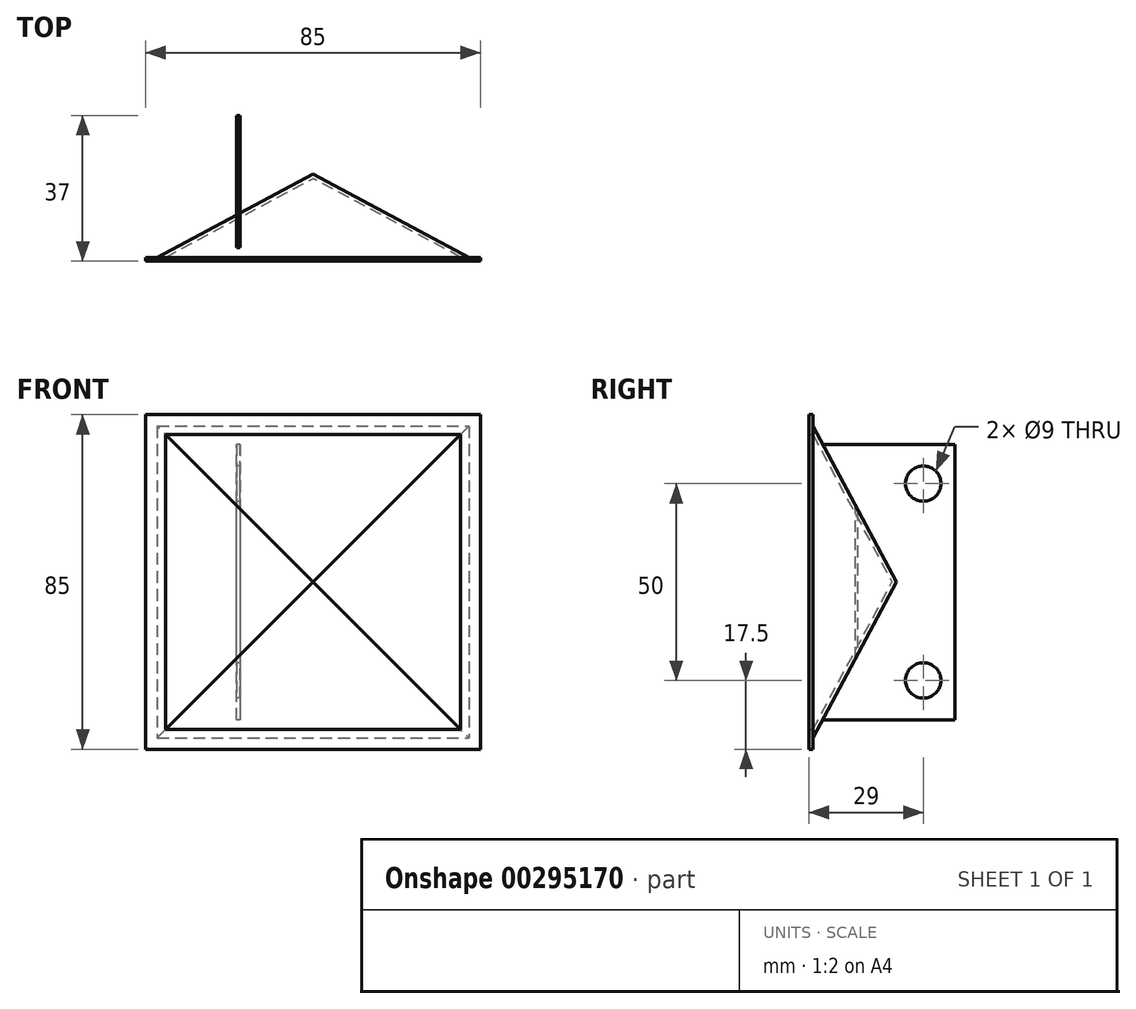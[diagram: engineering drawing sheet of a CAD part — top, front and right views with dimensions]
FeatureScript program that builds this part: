
annotation { "Feature Type Name" : "Feature", "Feature Type Description" : "" }
export const myFeature = defineFeature(function(context is Context, id is Id, definition is map)
    precondition{}
    {
        {
            var Q0;
            Q0=qCreatedBy(makeId("Front.planeOp"),FACE);
            var sketch = newSketch(context, id + "F0", { "sketchPlane" : qUnion([Q0])});
            skLineSegment(sketch, "E0.bottom", {"start": v(42.5, 42.5) * mm, "end": v(-42.5, 42.5) * mm});
            skLineSegment(sketch, "E0.top", {"start": v(42.5, -42.5) * mm, "end": v(-42.5, -42.5) * mm});
            skLineSegment(sketch, "E0.left", {"start": v(42.5, 42.5) * mm, "end": v(42.5, -42.5) * mm});
            skLineSegment(sketch, "E0.right", {"start": v(-42.5, 42.5) * mm, "end": v(-42.5, -42.5) * mm});
            skPoint(sketch, "E0.middle", {"position": v(0, 0) * mm});
            skLineSegment(sketch, "E1.bottom", {"start": v(-37.5, 37.5) * mm, "end": v(37.5, 37.5) * mm});
            skLineSegment(sketch, "E1.top", {"start": v(-37.5, -37.5) * mm, "end": v(37.5, -37.5) * mm});
            skLineSegment(sketch, "E1.left", {"start": v(-37.5, 37.5) * mm, "end": v(-37.5, -37.5) * mm});
            skLineSegment(sketch, "E1.right", {"start": v(37.5, 37.5) * mm, "end": v(37.5, -37.5) * mm});
            skSolve(sketch);
        }
        {
            var Q0;
            Q0=qCreatedBy(makeId("Front.planeOp"),FACE);
            cPlane(context, id + "F1", {"entities" : qUnion([Q0]), "cplaneType" : CPlaneType.OFFSET, "offset" : 20 * mm, "oppositeDirection" : true, "width" : 150 * mm, "height" : 150 * mm});
        }
        {
            var Q0;
            Q0=qCreatedBy(id+"F1.planeOp",FACE);
            var sketch = newSketch(context, id + "F2", { "sketchPlane" : qUnion([Q0])});
            skPoint(sketch, "E2", {"position": v(0, 0) * mm});
            skSolve(sketch);
        }
        {
            var Q0;
            Q0=makeQuery(id+"F0.imprint","IMPRINT",FACE,{"disambiguationData":[TD([[makeQuery(id+"F0.imprint","IMPRINT",EDGE,{"derivedFrom":sQuery(id+"F0.wireOp",EDGE,"E1.bottom")}),-1.0]])]});
            var Q1;
            Q1=sQuery(id+"F2.wireOp",VERTEX,"E2");
            loft(context, id + "F3", {"sheetProfilesArray" : [{ "sheetProfileEntities" : qUnion([Q0]) }, { "sheetProfileEntities" : qUnion([Q1]) }]});
        }
        {
            var Q0;
            Q0=makeQuery(id+"F3.opLoft","CAP_FACE",FACE,{"disambiguationData":[OSD([makeQuery(id+"F0.imprint","IMPRINT",FACE,{"disambiguationData":[TD([[makeQuery(id+"F0.imprint","IMPRINT",EDGE,{"derivedFrom":sQuery(id+"F0.wireOp",EDGE,"E1.bottom")}),-1.0]])]})])],"isStart":true});
            shell(context, id + "F4", {"entities" : qUnion([Q0]), "thickness" : 1 * mm, "oppositeDirection" : true});
        }
        {
            var Q0;
            Q0=makeQuery(id+"F0.imprint","IMPRINT",FACE,{"disambiguationData":[TD([[makeQuery(id+"F0.imprint","IMPRINT",EDGE,{"derivedFrom":sQuery(id+"F0.wireOp",EDGE,"E0.bottom")}),1.0]])]});
            extrude(context, id + "F5", {"entities" : qUnion([Q0]), "operationType" : NewBodyOperationType.ADD, "depth" : 1 * mm});
        }
        {
            var Q0;
            Q0=qCreatedBy(makeId("Front.planeOp"),FACE);
            cPlane(context, id + "F6", {"entities" : qUnion([Q0]), "cplaneType" : CPlaneType.OFFSET, "offset" : 36 * mm, "oppositeDirection" : true, "width" : 150 * mm, "height" : 150 * mm});
        }
        {
            var Q0;
            Q0=qCreatedBy(id+"F6.planeOp",FACE);
            var sketch = newSketch(context, id + "F7", { "sketchPlane" : qUnion([Q0])});
            skLineSegment(sketch, "E3", {"start": v(-19.5, -35) * mm, "end": v(-19.5, 35) * mm});
            skLineSegment(sketch, "E4", {"start": v(-19.5, 35) * mm, "end": v(-18.5, 35) * mm});
            skLineSegment(sketch, "E5", {"start": v(-18.5, 35) * mm, "end": v(-18.5, -35) * mm});
            skLineSegment(sketch, "E6", {"start": v(-18.5, -35) * mm, "end": v(-19.5, -35) * mm});
            skSolve(sketch);
        }
        {
            var Q0;
            Q0 = qSketchRegion(id + "F7", true);
            extrude(context, id + "F8", {"entities" : qUnion([Q0]), "operationType" : NewBodyOperationType.ADD, "endBound" : BoundingType.UP_TO_NEXT, "depth" : 25 * mm});
        }
        {
            var Q0;
            Q0=makeQuery(id+"F8.opExtrude","SWEPT_FACE",FACE,{"disambiguationData":[OSD([sQuery(id+"F7.wireOp",EDGE,"E3")])]});
            var sketch = newSketch(context, id + "F9", { "sketchPlane" : qUnion([Q0])});
            skCircle(sketch, "E7", {"center": v(-28, -25) * mm, "radius": 4.5 * mm});
            skCircle(sketch, "E8", {"center": v(-28, 25) * mm, "radius": 4.5 * mm});
            skSolve(sketch);
        }
        {
            var Q0;
            Q0 = qSketchRegion(id + "F9", true);
            extrude(context, id + "F10", {"entities" : qUnion([Q0]), "operationType" : NewBodyOperationType.REMOVE, "endBound" : BoundingType.THROUGH_ALL, "oppositeDirection" : true, "depth" : 25 * mm});
        }
    });
